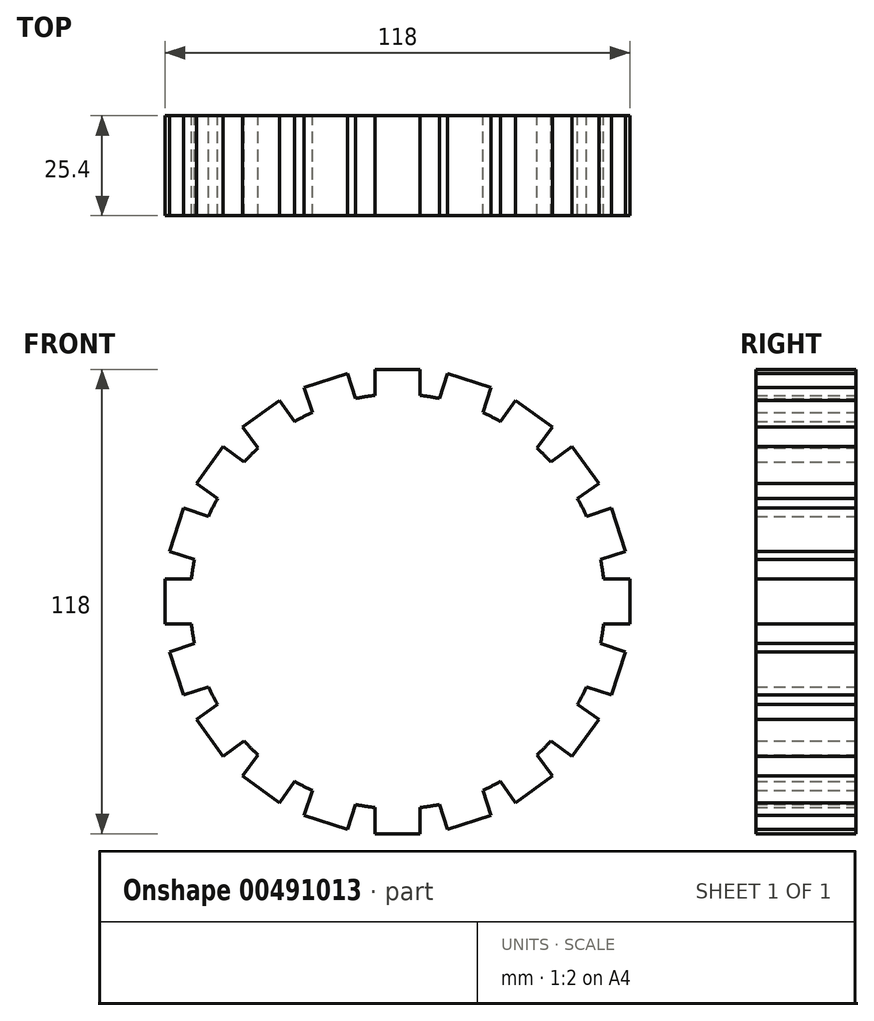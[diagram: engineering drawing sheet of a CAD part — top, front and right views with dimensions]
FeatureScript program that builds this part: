
annotation { "Feature Type Name" : "Feature", "Feature Type Description" : "" }
export const myFeature = defineFeature(function(context is Context, id is Id, definition is map)
    precondition{}
    {
        {
            var Q0;
            Q0=qCreatedBy(makeId("Front.planeOp"),FACE);
            var sketch = newSketch(context, id + "F0", { "sketchPlane" : qUnion([Q0])});
            skCircle(sketch, "E0", {"center": v(0, 0) * mm, "radius": 52.68 * mm, "construction": true});
            skLineSegment(sketch, "E1.bottom", {"start": v(5.76, 59) * mm, "end": v(-5.76, 59) * mm});
            skLineSegment(sketch, "E1.top", {"start": v(5.76, 46.35) * mm, "end": v(-5.76, 46.35) * mm});
            skLineSegment(sketch, "E1.left", {"start": v(5.76, 59) * mm, "end": v(5.76, 46.35) * mm});
            skLineSegment(sketch, "E1.right", {"start": v(-5.76, 59) * mm, "end": v(-5.76, 46.35) * mm});
            skPoint(sketch, "E1.middle", {"position": v(0, 52.68) * mm});
            skLineSegment(sketch, "E2.1.0", {"start": v(-12.76, 57.9) * mm, "end": v(-23.7, 54.33) * mm});
            skLineSegment(sketch, "E2.1.1", {"start": v(-12.76, 57.9) * mm, "end": v(-8.85, 45.86) * mm});
            skLineSegment(sketch, "E2.1.2", {"start": v(-8.85, 45.86) * mm, "end": v(-19.8, 42.3) * mm});
            skLineSegment(sketch, "E2.1.3", {"start": v(-23.7, 54.33) * mm, "end": v(-19.8, 42.3) * mm});
            skLineSegment(sketch, "E2.2.0", {"start": v(-30.02, 51.12) * mm, "end": v(-39.34, 44.35) * mm});
            skLineSegment(sketch, "E2.2.1", {"start": v(-30.02, 51.12) * mm, "end": v(-26.12, 45.74) * mm});
            skLineSegment(sketch, "E2.2.3", {"start": v(-39.34, 44.35) * mm, "end": v(-35.43, 38.98) * mm});
            skLineSegment(sketch, "E2.3.0", {"start": v(-44.35, 39.34) * mm, "end": v(-51.12, 30.02) * mm});
            skLineSegment(sketch, "E2.3.1", {"start": v(-44.35, 39.34) * mm, "end": v(-38.98, 35.43) * mm});
            skLineSegment(sketch, "E2.3.3", {"start": v(-51.12, 30.02) * mm, "end": v(-45.74, 26.12) * mm});
            skLineSegment(sketch, "E2.4.0", {"start": v(-54.33, 23.7) * mm, "end": v(-57.9, 12.76) * mm});
            skLineSegment(sketch, "E2.4.1", {"start": v(-54.33, 23.7) * mm, "end": v(-48.02, 21.65) * mm});
            skLineSegment(sketch, "E2.4.3", {"start": v(-57.9, 12.76) * mm, "end": v(-51.58, 10.7) * mm});
            skLineSegment(sketch, "E2.5.0", {"start": v(-59, 5.76) * mm, "end": v(-59, -5.76) * mm});
            skLineSegment(sketch, "E2.5.1", {"start": v(-59, 5.76) * mm, "end": v(-52.36, 5.76) * mm});
            skLineSegment(sketch, "E2.5.3", {"start": v(-59, -5.76) * mm, "end": v(-52.36, -5.76) * mm});
            skLineSegment(sketch, "E2.6.0", {"start": v(-57.9, -12.76) * mm, "end": v(-54.33, -23.7) * mm});
            skLineSegment(sketch, "E2.6.1", {"start": v(-57.9, -12.76) * mm, "end": v(-51.58, -10.7) * mm});
            skLineSegment(sketch, "E2.6.3", {"start": v(-54.33, -23.7) * mm, "end": v(-42.3, -19.8) * mm});
            skLineSegment(sketch, "E2.7.0", {"start": v(-51.12, -30.02) * mm, "end": v(-44.35, -39.34) * mm});
            skLineSegment(sketch, "E2.7.1", {"start": v(-51.12, -30.02) * mm, "end": v(-40.88, -22.59) * mm});
            skLineSegment(sketch, "E2.7.2", {"start": v(-40.88, -22.59) * mm, "end": v(-34.12, -31.9) * mm});
            skLineSegment(sketch, "E2.7.3", {"start": v(-44.35, -39.34) * mm, "end": v(-34.12, -31.9) * mm});
            skLineSegment(sketch, "E2.8.0", {"start": v(-39.34, -44.35) * mm, "end": v(-30.02, -51.12) * mm});
            skLineSegment(sketch, "E2.8.1", {"start": v(-39.34, -44.35) * mm, "end": v(-31.9, -34.12) * mm});
            skLineSegment(sketch, "E2.8.2", {"start": v(-31.9, -34.12) * mm, "end": v(-22.59, -40.88) * mm});
            skLineSegment(sketch, "E2.8.3", {"start": v(-30.02, -51.12) * mm, "end": v(-22.59, -40.88) * mm});
            skLineSegment(sketch, "E2.9.0", {"start": v(-23.7, -54.33) * mm, "end": v(-12.76, -57.9) * mm});
            skLineSegment(sketch, "E2.9.1", {"start": v(-23.7, -54.33) * mm, "end": v(-19.8, -42.3) * mm});
            skLineSegment(sketch, "E2.9.2", {"start": v(-19.8, -42.3) * mm, "end": v(-8.85, -45.86) * mm});
            skLineSegment(sketch, "E2.9.3", {"start": v(-12.76, -57.9) * mm, "end": v(-8.85, -45.86) * mm});
            skLineSegment(sketch, "E2.10.0", {"start": v(-5.76, -59) * mm, "end": v(5.76, -59) * mm});
            skLineSegment(sketch, "E2.10.1", {"start": v(-5.76, -59) * mm, "end": v(-5.76, -46.35) * mm});
            skLineSegment(sketch, "E2.10.2", {"start": v(-5.76, -46.35) * mm, "end": v(5.76, -46.35) * mm});
            skLineSegment(sketch, "E2.10.3", {"start": v(5.76, -59) * mm, "end": v(5.76, -46.35) * mm});
            skLineSegment(sketch, "E2.11.0", {"start": v(12.76, -57.9) * mm, "end": v(23.7, -54.33) * mm});
            skLineSegment(sketch, "E2.11.1", {"start": v(12.76, -57.9) * mm, "end": v(8.85, -45.86) * mm});
            skLineSegment(sketch, "E2.11.2", {"start": v(8.85, -45.86) * mm, "end": v(19.8, -42.3) * mm});
            skLineSegment(sketch, "E2.11.3", {"start": v(23.7, -54.33) * mm, "end": v(19.8, -42.3) * mm});
            skLineSegment(sketch, "E2.12.0", {"start": v(30.02, -51.12) * mm, "end": v(39.34, -44.35) * mm});
            skLineSegment(sketch, "E2.12.1", {"start": v(30.02, -51.12) * mm, "end": v(22.59, -40.88) * mm});
            skLineSegment(sketch, "E2.12.2", {"start": v(22.59, -40.88) * mm, "end": v(31.9, -34.12) * mm});
            skLineSegment(sketch, "E2.12.3", {"start": v(39.34, -44.35) * mm, "end": v(31.9, -34.12) * mm});
            skLineSegment(sketch, "E2.13.0", {"start": v(44.35, -39.34) * mm, "end": v(51.12, -30.02) * mm});
            skLineSegment(sketch, "E2.13.1", {"start": v(44.35, -39.34) * mm, "end": v(34.12, -31.9) * mm});
            skLineSegment(sketch, "E2.13.2", {"start": v(34.12, -31.9) * mm, "end": v(40.88, -22.59) * mm});
            skLineSegment(sketch, "E2.13.3", {"start": v(51.12, -30.02) * mm, "end": v(40.88, -22.59) * mm});
            skLineSegment(sketch, "E2.14.0", {"start": v(54.33, -23.7) * mm, "end": v(57.9, -12.76) * mm});
            skLineSegment(sketch, "E2.14.1", {"start": v(54.33, -23.7) * mm, "end": v(42.3, -19.8) * mm});
            skLineSegment(sketch, "E2.14.2", {"start": v(42.3, -19.8) * mm, "end": v(45.86, -8.85) * mm});
            skLineSegment(sketch, "E2.14.3", {"start": v(57.9, -12.76) * mm, "end": v(45.86, -8.85) * mm});
            skLineSegment(sketch, "E2.15.0", {"start": v(59, -5.76) * mm, "end": v(59, 5.76) * mm});
            skLineSegment(sketch, "E2.15.1", {"start": v(59, -5.76) * mm, "end": v(46.35, -5.76) * mm});
            skLineSegment(sketch, "E2.15.2", {"start": v(46.35, -5.76) * mm, "end": v(46.35, 5.76) * mm});
            skLineSegment(sketch, "E2.15.3", {"start": v(59, 5.76) * mm, "end": v(46.35, 5.76) * mm});
            skLineSegment(sketch, "E2.16.0", {"start": v(57.9, 12.76) * mm, "end": v(54.33, 23.7) * mm});
            skLineSegment(sketch, "E2.16.1", {"start": v(57.9, 12.76) * mm, "end": v(45.86, 8.85) * mm});
            skLineSegment(sketch, "E2.16.2", {"start": v(45.86, 8.85) * mm, "end": v(42.3, 19.8) * mm});
            skLineSegment(sketch, "E2.16.3", {"start": v(54.33, 23.7) * mm, "end": v(42.3, 19.8) * mm});
            skLineSegment(sketch, "E2.17.0", {"start": v(51.12, 30.02) * mm, "end": v(44.35, 39.34) * mm});
            skLineSegment(sketch, "E2.17.1", {"start": v(51.12, 30.02) * mm, "end": v(40.88, 22.59) * mm});
            skLineSegment(sketch, "E2.17.2", {"start": v(40.88, 22.59) * mm, "end": v(34.12, 31.9) * mm});
            skLineSegment(sketch, "E2.17.3", {"start": v(44.35, 39.34) * mm, "end": v(34.12, 31.9) * mm});
            skLineSegment(sketch, "E2.18.0", {"start": v(39.34, 44.35) * mm, "end": v(30.02, 51.12) * mm});
            skLineSegment(sketch, "E2.18.1", {"start": v(39.34, 44.35) * mm, "end": v(31.9, 34.12) * mm});
            skLineSegment(sketch, "E2.18.2", {"start": v(31.9, 34.12) * mm, "end": v(22.59, 40.88) * mm});
            skLineSegment(sketch, "E2.18.3", {"start": v(30.02, 51.12) * mm, "end": v(22.59, 40.88) * mm});
            skLineSegment(sketch, "E2.19.0", {"start": v(23.7, 54.33) * mm, "end": v(12.76, 57.9) * mm});
            skLineSegment(sketch, "E2.19.1", {"start": v(23.7, 54.33) * mm, "end": v(19.8, 42.3) * mm});
            skLineSegment(sketch, "E2.19.2", {"start": v(19.8, 42.3) * mm, "end": v(8.85, 45.86) * mm});
            skLineSegment(sketch, "E2.19.3", {"start": v(12.76, 57.9) * mm, "end": v(8.85, 45.86) * mm});
            skCircle(sketch, "E3", {"center": v(0, 0) * mm, "radius": 52.68 * mm});
            skPoint(sketch, "E4.orphan", {"position": v(-31.9, 34.12) * mm});
            skPoint(sketch, "E5.orphan", {"position": v(-22.59, 40.88) * mm});
            skPoint(sketch, "E6.orphan", {"position": v(-40.88, 22.59) * mm});
            skPoint(sketch, "E7.orphan", {"position": v(-45.86, 8.85) * mm});
            skPoint(sketch, "E8.orphan", {"position": v(-46.35, -5.76) * mm});
            skSolve(sketch);
        }
        {
            var Q0;
            Q0 = qSketchRegion(id + "F0", true);
            extrude(context, id + "F1", {"entities" : qUnion([Q0]), "depth" : 25.4 * mm});
        }
    });
